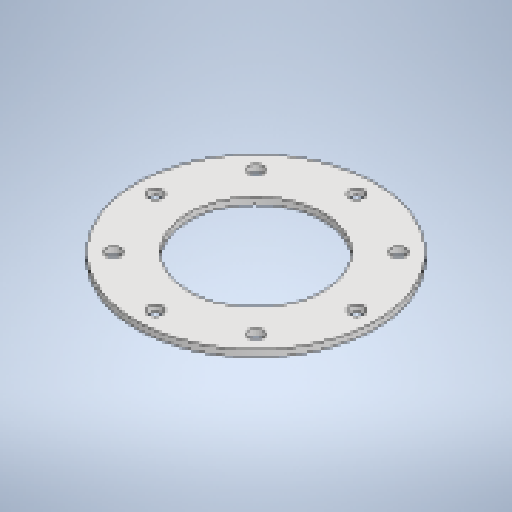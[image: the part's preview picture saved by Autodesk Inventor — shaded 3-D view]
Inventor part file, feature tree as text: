
AUTODESK INVENTOR PART (.ipt)
format: ipt  version: 2025.1 (Build 291241020, 241B)  size: 207,872 bytes
history: native  units: mm
features: other x3, sketch x2, sheet_metal_op x1, pattern_circular x1
ambient origin geometry x8: Origin, YZ Plane, XZ Plane, XY Plane, X Axis, Y Axis, Z Axis, Center Point
bodies: Body1 (feature_tree)
feature tree (7):
  sheet_metal_op  "Face2"
  pattern_circular  "Circular Pattern1"  [2 undecoded]
  sketch  "Sketch2"  dims[d14=8.0mm]
  other  "Plate2"
  sketch  "Sketch3"  dims[d15=17.0mm d17=8.0mm d18=0.0mm d19=80.0mm d20=360.0deg d25=161.0mm d27=285.0mm d28=240.0mm]
  other  "Cut1"
  other  "Definition1"
note: 2 required parameter values undecoded (feature->parameter linkage not recoverable at this tier; creation-order binding heuristic only, values carry confidence <= 0.55)
